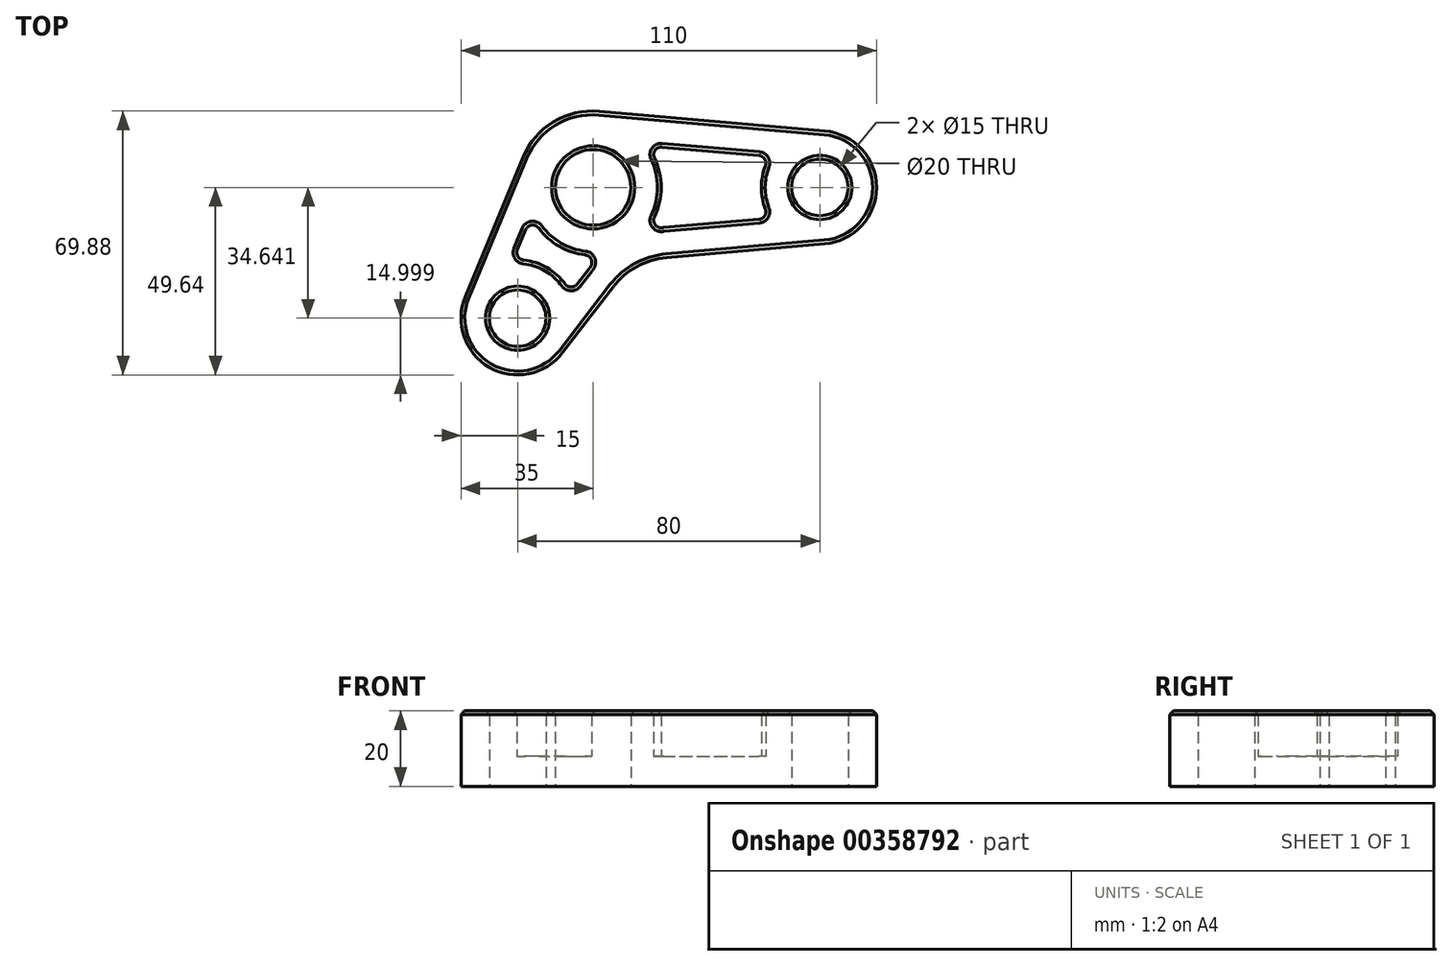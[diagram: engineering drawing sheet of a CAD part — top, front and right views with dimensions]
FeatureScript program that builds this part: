
annotation { "Feature Type Name" : "Feature", "Feature Type Description" : "" }
export const myFeature = defineFeature(function(context is Context, id is Id, definition is map)
    precondition{}
    {
        {
            var Q0;
            Q0=qCreatedBy(makeId("Top.planeOp"),FACE);
            var sketch = newSketch(context, id + "F0", { "sketchPlane" : qUnion([Q0])});
            skLineSegment(sketch, "E0", {"start": v(0, 0) * mm, "end": v(60, 0) * mm, "construction": true});
            skLineSegment(sketch, "E1", {"start": v(0, 0) * mm, "end": v(-20, -34.64) * mm, "construction": true});
            skCircle(sketch, "E2", {"center": v(-20, -34.64) * mm, "radius": 7.5 * mm});
            skCircle(sketch, "E3", {"center": v(0, 0) * mm, "radius": 10 * mm});
            skCircle(sketch, "E4", {"center": v(60, 0) * mm, "radius": 7.5 * mm});
            skLineSegment(sketch, "E5", {"start": v(-33.86, -28.9) * mm, "end": v(-18.62, 7.9) * mm});
            skLineSegment(sketch, "E6", {"start": v(1.6, 20.17) * mm, "end": v(61.3, 14.94) * mm});
            skLineSegment(sketch, "E7", {"start": v(-8.1, -43.77) * mm, "end": v(10.62, -19.38) * mm});
            skLineSegment(sketch, "E8", {"start": v(10.62, -19.38) * mm, "end": v(61.3, -14.94) * mm});
            skArc(sketch, "E9", {"start": v(-33.86, -28.9) * mm, "mid": v(-27.5, -47.63) * mm, "end": v(-8.1, -43.77) * mm});
            skArc(sketch, "E10", {"start": v(61.3, -14.94) * mm, "mid": v(75, 0) * mm, "end": v(61.3, 14.94) * mm});
            skPoint(sketch, "E11.visualSharp", {"position": v(-13, 21.44) * mm});
            skArc(sketch, "E11.filletArc", {"start": v(1.6, 20.17) * mm, "mid": v(-10.51, 17.34) * mm, "end": v(-18.62, 7.9) * mm});
            skSolve(sketch);
        }
        {
            var Q0;
            Q0=makeQuery(id+"F0.imprint","IMPRINT",FACE,{"disambiguationData":[TD([[makeQuery(id+"F0.imprint","IMPRINT",EDGE,{"derivedFrom":sQuery(id+"F0.wireOp",EDGE,"E2")}),-1.0]])]});
            extrude(context, id + "F1", {"entities" : qUnion([Q0]), "depth" : 20 * mm});
        }
        {
            var Q0;
            Q0=makeQuery(id+"F1.opExtrude","SWEPT_EDGE",EDGE,{"disambiguationData":[OSD([sQuery(id+"F0.wireOp",EDGE,"E7"),sQuery(id+"F0.wireOp",EDGE,"E8")])]});
            fillet(context, id + "F2", {"entities" : qUnion([Q0]), "radius" : 20 * mm, "tangentPropagation" : true, "allowEdgeOverflow" : false});
        }
        {
            var Q0;
            Q0=makeQuery(id+"F1.opExtrude","CAP_FACE",FACE,{"disambiguationData":[OSD([sQuery(id+"F0.wireOp",EDGE,"E2"),sQuery(id+"F0.wireOp",EDGE,"E3"),sQuery(id+"F0.wireOp",EDGE,"E4"),sQuery(id+"F0.wireOp",EDGE,"E5"),sQuery(id+"F0.wireOp",EDGE,"E6"),sQuery(id+"F0.wireOp",EDGE,"E7"),sQuery(id+"F0.wireOp",EDGE,"E8"),sQuery(id+"F0.wireOp",EDGE,"E9"),sQuery(id+"F0.wireOp",EDGE,"E10"),sQuery(id+"F0.wireOp",EDGE,"E11.filletArc")])],"isStart":false});
            shell(context, id + "F3", {"entities" : qUnion([Q0]), "thickness" : 8 * mm});
        }
        {
            var Q0;
            Q0=makeQuery(id+"F3.opShell","TWEAK_EDGE",EDGE,{"derivedFrom":[makeQuery(id+"F1.opExtrude","SWEPT_FACE",FACE,{"disambiguationData":[OSD([sQuery(id+"F0.wireOp",EDGE,"E3")])]}),makeQuery(id+"F1.opExtrude","SWEPT_FACE",FACE,{"disambiguationData":[OSD([sQuery(id+"F0.wireOp",EDGE,"E6")])]})]});
            fillet(context, id + "F4", {"entities" : qUnion([Q0]), "radius" : 2 * mm, "tangentPropagation" : true, "allowEdgeOverflow" : false});
        }
        {
            var Q0;
            Q0=makeQuery(id+"F3.opShell","TWEAK_EDGE",EDGE,{"disambiguationData":[OD(1.0)],"derivedFrom":[makeQuery(id+"F1.opExtrude","SWEPT_FACE",FACE,{"disambiguationData":[OSD([sQuery(id+"F0.wireOp",EDGE,"E3")])]}),makeQuery(id+"F2.opFillet","BLEND_FACE",FACE,{"disambiguationData":[OSD([sQuery(id+"F0.wireOp",EDGE,"E7"),sQuery(id+"F0.wireOp",EDGE,"E8")])]})]});
            var Q1;
            Q1=makeQuery(id+"F3.opShell","TWEAK_EDGE",EDGE,{"derivedFrom":[makeQuery(id+"F1.opExtrude","SWEPT_FACE",FACE,{"disambiguationData":[OSD([sQuery(id+"F0.wireOp",EDGE,"E3")])]}),makeQuery(id+"F1.opExtrude","SWEPT_FACE",FACE,{"disambiguationData":[OSD([sQuery(id+"F0.wireOp",EDGE,"E5")])]})]});
            var Q2;
            Q2=makeQuery(id+"F3.opShell","TWEAK_EDGE",EDGE,{"derivedFrom":[makeQuery(id+"F1.opExtrude","SWEPT_FACE",FACE,{"disambiguationData":[OSD([sQuery(id+"F0.wireOp",EDGE,"E2")])]}),makeQuery(id+"F1.opExtrude","SWEPT_FACE",FACE,{"disambiguationData":[OSD([sQuery(id+"F0.wireOp",EDGE,"E5")])]})]});
            var Q3;
            Q3=makeQuery(id+"F3.opShell","TWEAK_EDGE",EDGE,{"derivedFrom":[makeQuery(id+"F1.opExtrude","SWEPT_FACE",FACE,{"disambiguationData":[OSD([sQuery(id+"F0.wireOp",EDGE,"E2")])]}),makeQuery(id+"F1.opExtrude","SWEPT_FACE",FACE,{"disambiguationData":[OSD([sQuery(id+"F0.wireOp",EDGE,"E7")])]})]});
            var Q4;
            Q4=makeQuery(id+"F3.opShell","TWEAK_EDGE",EDGE,{"disambiguationData":[OD(0.0)],"derivedFrom":[makeQuery(id+"F1.opExtrude","SWEPT_FACE",FACE,{"disambiguationData":[OSD([sQuery(id+"F0.wireOp",EDGE,"E3")])]}),makeQuery(id+"F2.opFillet","BLEND_FACE",FACE,{"disambiguationData":[OSD([sQuery(id+"F0.wireOp",EDGE,"E7"),sQuery(id+"F0.wireOp",EDGE,"E8")])]})]});
            var Q5;
            Q5=makeQuery(id+"F3.opShell","TWEAK_EDGE",EDGE,{"derivedFrom":[makeQuery(id+"F1.opExtrude","SWEPT_FACE",FACE,{"disambiguationData":[OSD([sQuery(id+"F0.wireOp",EDGE,"E4")])]}),makeQuery(id+"F1.opExtrude","SWEPT_FACE",FACE,{"disambiguationData":[OSD([sQuery(id+"F0.wireOp",EDGE,"E8")])]})]});
            var Q6;
            Q6=makeQuery(id+"F3.opShell","TWEAK_EDGE",EDGE,{"derivedFrom":[makeQuery(id+"F1.opExtrude","SWEPT_FACE",FACE,{"disambiguationData":[OSD([sQuery(id+"F0.wireOp",EDGE,"E4")])]}),makeQuery(id+"F1.opExtrude","SWEPT_FACE",FACE,{"disambiguationData":[OSD([sQuery(id+"F0.wireOp",EDGE,"E6")])]})]});
            fillet(context, id + "F5", {"entities" : qUnion([Q0, Q1, Q2, Q3, Q4, Q5, Q6]), "radius" : 2 * mm, "tangentPropagation" : true, "allowEdgeOverflow" : false});
        }
        {
            var Q0;
            Q0=makeQuery(id+"F1.opExtrude","CAP_EDGE",EDGE,{"disambiguationData":[OSD([sQuery(id+"F0.wireOp",EDGE,"E8")])],"isStart":false});
            var Q1;
            Q1=makeQuery(id+"F1.opExtrude","CAP_EDGE",EDGE,{"disambiguationData":[OSD([sQuery(id+"F0.wireOp",EDGE,"E3")])],"isStart":false});
            var Q2;
            {var subQ0=sQuery(id+"F0.wireOp",EDGE,"E8");Q2=makeQuery(id+"F3.opShell","OFFSET_EDGE",EDGE,{"disambiguationData":[OSD([subQ0]),TDD([makeQuery(id+"F1.opExtrude","CAP_EDGE",EDGE,{"disambiguationData":[OSD([subQ0])],"isStart":false})])]});}
            var Q3;
            {var subQ0=sQuery(id+"F0.wireOp",EDGE,"E6");Q3=makeQuery(id+"F3.opShell","OFFSET_EDGE",EDGE,{"disambiguationData":[OSD([subQ0]),TDD([makeQuery(id+"F1.opExtrude","CAP_EDGE",EDGE,{"disambiguationData":[OSD([subQ0])],"isStart":false})])]});}
            var Q4;
            {var subQ0=sQuery(id+"F0.wireOp",EDGE,"E3");Q4=makeQuery(id+"F3.opShell","OFFSET_EDGE",EDGE,{"disambiguationData":[OSD([subQ0]),TDD([makeQuery(id+"F1.opExtrude","CAP_EDGE",EDGE,{"disambiguationData":[OSD([subQ0])],"isStart":false})]),OD(1.0)]});}
            var Q5;
            {var subQ0=sQuery(id+"F0.wireOp",EDGE,"E4");Q5=makeQuery(id+"F3.opShell","OFFSET_EDGE",EDGE,{"disambiguationData":[OSD([subQ0]),TDD([makeQuery(id+"F1.opExtrude","CAP_EDGE",EDGE,{"disambiguationData":[OSD([subQ0])],"isStart":false})])]});}
            var Q6;
            Q6=makeQuery(id+"F1.opExtrude","CAP_EDGE",EDGE,{"disambiguationData":[OSD([sQuery(id+"F0.wireOp",EDGE,"E2")])],"isStart":false});
            var Q7;
            {var subQ0=sQuery(id+"F0.wireOp",EDGE,"E2");Q7=makeQuery(id+"F3.opShell","OFFSET_EDGE",EDGE,{"disambiguationData":[OSD([subQ0]),TDD([makeQuery(id+"F1.opExtrude","CAP_EDGE",EDGE,{"disambiguationData":[OSD([subQ0])],"isStart":false})])]});}
            var Q8;
            {var subQ0=sQuery(id+"F0.wireOp",EDGE,"E7");Q8=makeQuery(id+"F3.opShell","OFFSET_EDGE",EDGE,{"disambiguationData":[OSD([subQ0]),TDD([makeQuery(id+"F1.opExtrude","CAP_EDGE",EDGE,{"disambiguationData":[OSD([subQ0])],"isStart":false})])]});}
            var Q9;
            {var subQ0=sQuery(id+"F0.wireOp",EDGE,"E11.filletArc");var subQ1=sQuery(id+"F0.wireOp",EDGE,"E10");var subQ2=sQuery(id+"F0.wireOp",EDGE,"E9");var subQ3=sQuery(id+"F0.wireOp",EDGE,"E8");var subQ4=sQuery(id+"F0.wireOp",EDGE,"E7");var subQ5=sQuery(id+"F0.wireOp",EDGE,"E6");var subQ6=sQuery(id+"F0.wireOp",EDGE,"E5");var subQ7=sQuery(id+"F0.wireOp",EDGE,"E4");var subQ8=sQuery(id+"F0.wireOp",EDGE,"E3");var subQ9=sQuery(id+"F0.wireOp",EDGE,"E2");Q9=makeQuery(id+"F3.opShell","OFFSET_EDGE",EDGE,{"disambiguationData":[OSD([subQ9,subQ8,subQ7,subQ6,subQ5,subQ4,subQ3,subQ2,subQ1,subQ0]),TDD([makeQuery(id+"F2.opFillet","BLEND_EDGE",EDGE,{"blendedFrom":[makeQuery(id+"F1.opExtrude","SWEPT_EDGE",EDGE,{"disambiguationData":[OSD([subQ4,subQ3])]}),makeQuery(id+"F1.opExtrude","CAP_FACE",FACE,{"disambiguationData":[OSD([subQ9,subQ8,subQ7,subQ6,subQ5,subQ4,subQ3,subQ2,subQ1,subQ0])],"isStart":false})],"blendedInto":[makeQuery(id+"F1.opExtrude","CAP_FACE",FACE,{"disambiguationData":[OSD([subQ9,subQ8,subQ7,subQ6,subQ5,subQ4,subQ3,subQ2,subQ1,subQ0])],"isStart":false})]})]),OD(0.0)]});}
            var Q10;
            {var subQ0=sQuery(id+"F0.wireOp",EDGE,"E3");Q10=makeQuery(id+"F3.opShell","OFFSET_EDGE",EDGE,{"disambiguationData":[OSD([subQ0]),TDD([makeQuery(id+"F1.opExtrude","CAP_EDGE",EDGE,{"disambiguationData":[OSD([subQ0])],"isStart":false})]),OD(0.0)]});}
            var Q11;
            {var subQ0=sQuery(id+"F0.wireOp",EDGE,"E5");Q11=makeQuery(id+"F3.opShell","OFFSET_EDGE",EDGE,{"disambiguationData":[OSD([subQ0]),TDD([makeQuery(id+"F1.opExtrude","CAP_EDGE",EDGE,{"disambiguationData":[OSD([subQ0])],"isStart":false})])]});}
            var Q12;
            Q12=makeQuery(id+"F1.opExtrude","CAP_EDGE",EDGE,{"disambiguationData":[OSD([sQuery(id+"F0.wireOp",EDGE,"E4")])],"isStart":false});
            var Q13;
            {var subQ0=sQuery(id+"F0.wireOp",EDGE,"E11.filletArc");var subQ1=sQuery(id+"F0.wireOp",EDGE,"E10");var subQ2=sQuery(id+"F0.wireOp",EDGE,"E9");var subQ3=sQuery(id+"F0.wireOp",EDGE,"E8");var subQ4=sQuery(id+"F0.wireOp",EDGE,"E7");var subQ5=sQuery(id+"F0.wireOp",EDGE,"E6");var subQ6=sQuery(id+"F0.wireOp",EDGE,"E5");var subQ7=sQuery(id+"F0.wireOp",EDGE,"E4");var subQ8=sQuery(id+"F0.wireOp",EDGE,"E3");var subQ9=sQuery(id+"F0.wireOp",EDGE,"E2");Q13=makeQuery(id+"F3.opShell","OFFSET_EDGE",EDGE,{"disambiguationData":[OSD([subQ9,subQ8,subQ7,subQ6,subQ5,subQ4,subQ3,subQ2,subQ1,subQ0]),TDD([makeQuery(id+"F2.opFillet","BLEND_EDGE",EDGE,{"blendedFrom":[makeQuery(id+"F1.opExtrude","SWEPT_EDGE",EDGE,{"disambiguationData":[OSD([subQ4,subQ3])]}),makeQuery(id+"F1.opExtrude","CAP_FACE",FACE,{"disambiguationData":[OSD([subQ9,subQ8,subQ7,subQ6,subQ5,subQ4,subQ3,subQ2,subQ1,subQ0])],"isStart":false})],"blendedInto":[makeQuery(id+"F1.opExtrude","CAP_FACE",FACE,{"disambiguationData":[OSD([subQ9,subQ8,subQ7,subQ6,subQ5,subQ4,subQ3,subQ2,subQ1,subQ0])],"isStart":false})]})]),OD(1.0)]});}
            chamfer(context, id + "F6", {"entities" : qUnion([Q0, Q1, Q2, Q3, Q4, Q5, Q6, Q7, Q8, Q9, Q10, Q11, Q12, Q13]), "width" : 1 * mm, "tangentPropagation" : true});
        }
    });
